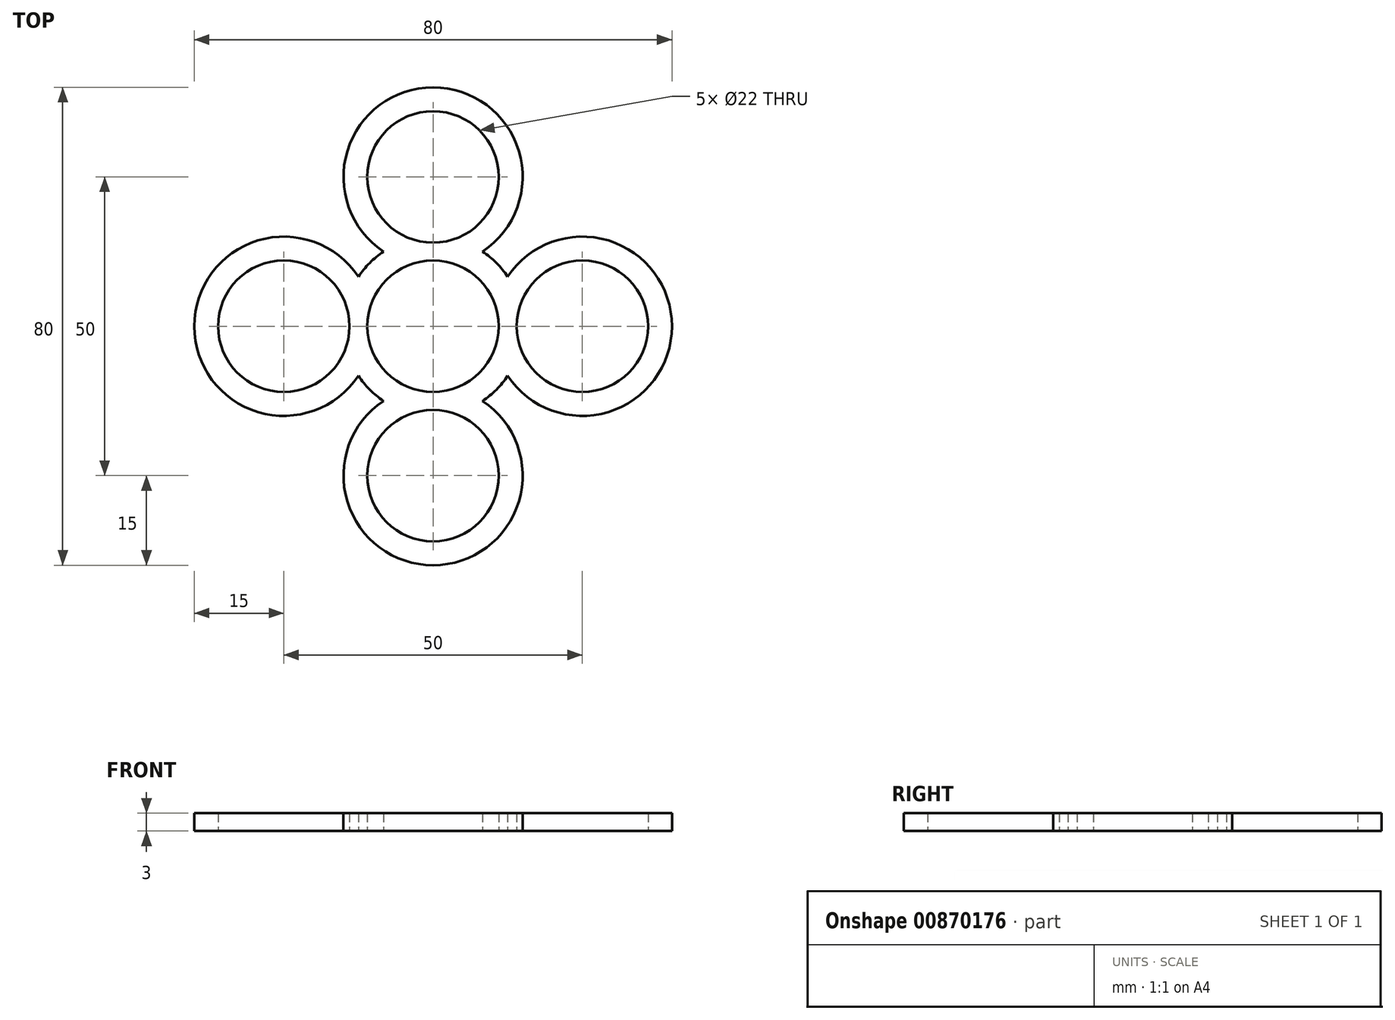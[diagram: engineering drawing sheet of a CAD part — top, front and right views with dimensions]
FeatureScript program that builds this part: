
annotation { "Feature Type Name" : "Feature", "Feature Type Description" : "" }
export const myFeature = defineFeature(function(context is Context, id is Id, definition is map)
    precondition{}
    {
        {
            var Q0;
            Q0=qCreatedBy(makeId("Top.planeOp"),FACE);
            var sketch = newSketch(context, id + "F0", { "sketchPlane" : qUnion([Q0])});
            skCircle(sketch, "E0", {"center": v(0, 0) * mm, "radius": 11 * mm});
            skArc(sketch, "E1", {"start": v(-12.5, -8.3) * mm, "mid": v(-10.6, -10.6) * mm, "end": v(-8.3, -12.5) * mm});
            skLineSegment(sketch, "E2", {"start": v(-10, 0) * mm, "end": v(-11, 0) * mm});
            skCircle(sketch, "E3", {"center": v(-25, 0) * mm, "radius": 11 * mm});
            skArc(sketch, "E4", {"start": v(-12.5, 8.3) * mm, "mid": v(-40, 0) * mm, "end": v(-12.5, -8.3) * mm});
            skLineSegment(sketch, "E5", {"start": v(0, 10) * mm, "end": v(0, 15) * mm});
            skCircle(sketch, "E6", {"center": v(0, 25) * mm, "radius": 11 * mm});
            skArc(sketch, "E7", {"start": v(8.3, 12.5) * mm, "mid": v(0, 40) * mm, "end": v(-8.3, 12.5) * mm});
            skLineSegment(sketch, "E8", {"start": v(0, -10) * mm, "end": v(0, -15) * mm});
            skCircle(sketch, "E9", {"center": v(0, -25) * mm, "radius": 11 * mm});
            skArc(sketch, "E10", {"start": v(-8.3, -12.5) * mm, "mid": v(0, -40) * mm, "end": v(8.3, -12.5) * mm});
            skArc(sketch, "E11.trimOffspring", {"start": v(8.3, -12.5) * mm, "mid": v(10.6, -10.6) * mm, "end": v(12.5, -8.3) * mm});
            skArc(sketch, "E12.trimOffspring", {"start": v(-8.3, 12.5) * mm, "mid": v(-10.6, 10.6) * mm, "end": v(-12.5, 8.3) * mm});
            skCircle(sketch, "E13", {"center": v(25, 0) * mm, "radius": 11 * mm});
            skArc(sketch, "E14", {"start": v(12.5, -8.3) * mm, "mid": v(40, 0) * mm, "end": v(12.5, 8.3) * mm});
            skArc(sketch, "E15.trimOffspring", {"start": v(12.5, 8.3) * mm, "mid": v(10.6, 10.6) * mm, "end": v(8.3, 12.5) * mm});
            skLineSegment(sketch, "E16.trimOffspring", {"start": v(-14, 0) * mm, "end": v(-15, 0) * mm});
            skSolve(sketch);
        }
        {
            var Q0;
            Q0 = qSketchRegion(id + "F0", true);
            extrude(context, id + "F1", {"entities" : qUnion([Q0]), "depth" : 3 * mm, "offsetDistance" : 25.4 * mm});
        }
    });
